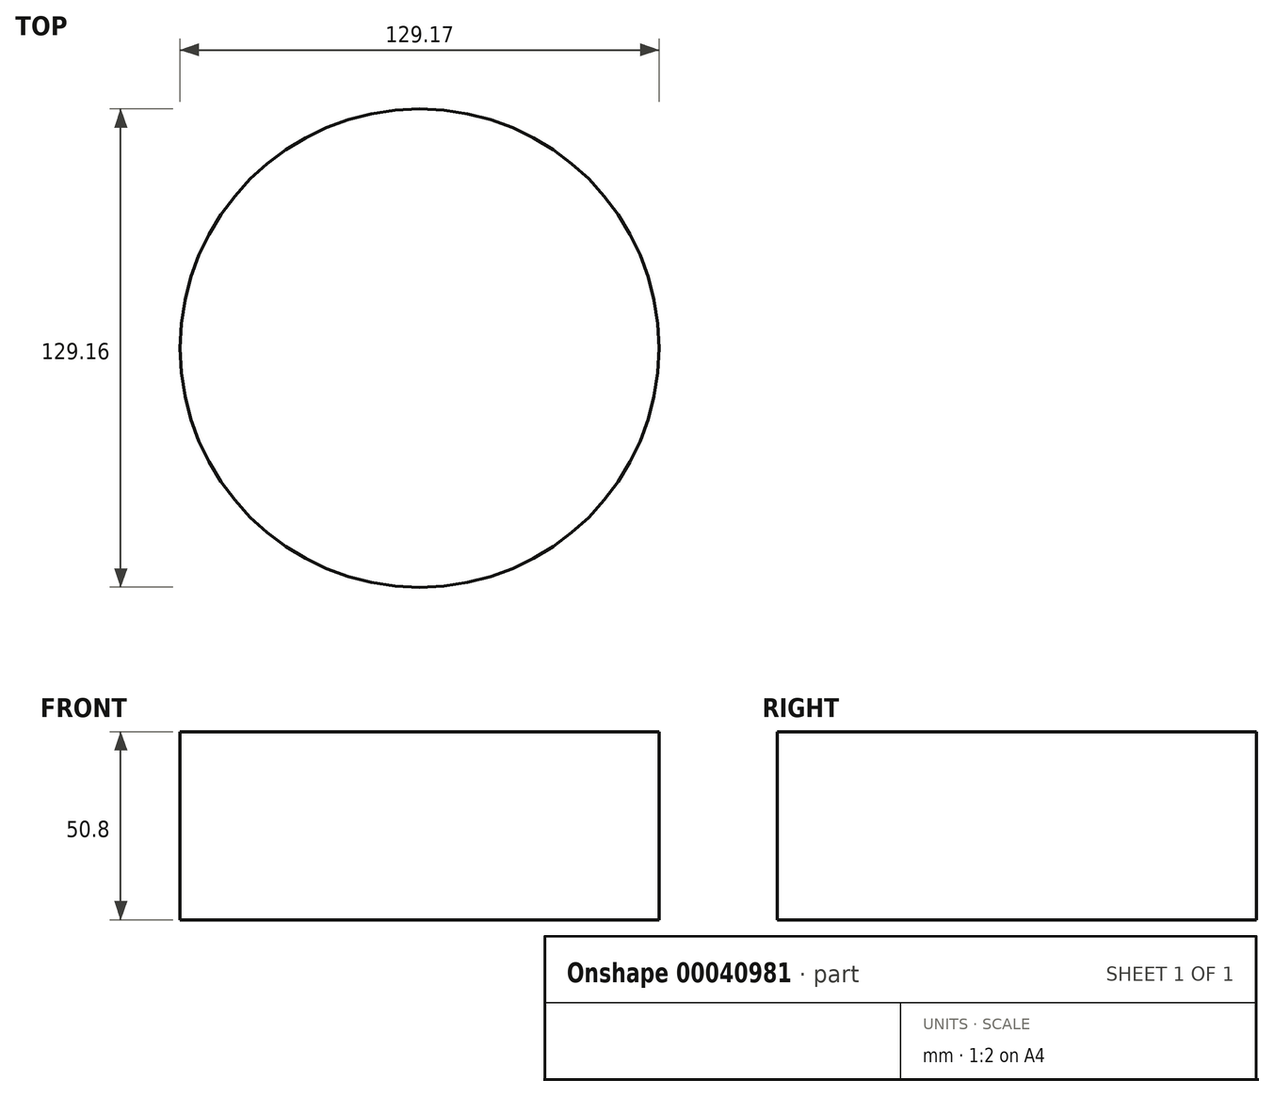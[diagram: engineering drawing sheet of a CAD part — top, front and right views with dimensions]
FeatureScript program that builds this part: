
annotation { "Feature Type Name" : "Feature", "Feature Type Description" : "" }
export const myFeature = defineFeature(function(context is Context, id is Id, definition is map)
    precondition{}
    {
        {
            var Q0;
            Q0=qCreatedBy(makeId("Top.planeOp"),FACE);
            var sketch = newSketch(context, id + "F0", { "sketchPlane" : qUnion([Q0])});
            skCircle(sketch, "E0", {"center": v(-59, 34.7) * mm, "radius": 64.58 * mm});
            skSolve(sketch);
        }
        {
            var Q0;
            Q0=makeQuery(id+"F0.imprint","IMPRINT",FACE,{"disambiguationData":[TD([[makeQuery(id+"F0.imprint","IMPRINT",EDGE,{"derivedFrom":sQuery(id+"F0.wireOp",EDGE,"E0")}),1.0]])]});
            extrude(context, id + "F1", {"entities" : qUnion([Q0]), "depth" : 25.4 * mm});
        }
        {
            var Q0;
            Q0=makeQuery(id+"F1.opExtrude","CAP_FACE",FACE,{"disambiguationData":[OSD([sQuery(id+"F0.wireOp",EDGE,"E0")])],"isStart":false});
            var sketch = newSketch(context, id + "F2", { "sketchPlane" : qUnion([Q0])});
            skSolve(sketch);
        }
        {
            var Q0;
            Q0=makeQuery(id+"F2.imprint","IMPRINT",FACE,{"disambiguationData":[TD([[makeQuery(id+"F2.imprint","IMPRINT",EDGE,{"derivedFrom":makeQuery(id+"F1.opExtrude","CAP_EDGE",EDGE,{"disambiguationData":[OSD([sQuery(id+"F0.wireOp",EDGE,"E0")])],"isStart":false})}),1.0]])]});
            extrude(context, id + "F3", {"entities" : qUnion([Q0]), "operationType" : NewBodyOperationType.ADD, "depth" : 25.4 * mm});
        }
    });
